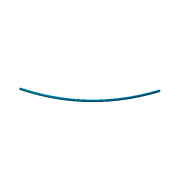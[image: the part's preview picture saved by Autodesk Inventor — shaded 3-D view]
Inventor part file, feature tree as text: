
AUTODESK INVENTOR PART (.ipt)
format: ipt  version: 2016 (Build 200138000, 138)  size: 222,208 bytes
history: native  units: in
note: dims shown in document units (in); Inventor stores cm internally (conversion verified against a paired STEP export)
features: sketch x6, extrude x3, sweep x2, other x2, plane x1
ambient origin geometry x8: Origin, YZ Plane, XZ Plane, XY Plane, X Axis, Y Axis, Z Axis, Center Point
bodies: Body1 (feature_tree)
feature tree (14):
  sweep  "FullSpar"
  sweep  "removeFirstPart"
  extrude  "Extrusion10"  TaperAngle=0.0deg  [1 undecoded]
  extrude  "Extrusion12"  Depth=0.3937in TaperAngle=0.0deg
  sketch  "Sketch21"  dims[d48=0.2756in d49=7.874in d50=0.0in]
  plane  "Work Plane1"
  extrude  "Extrusion13"  Depth=7.874in TaperAngle=0.0deg
  other  "2D Equation Curve1"
  sketch  "Sketch4"  dims[d0=0.0in d1=270.0in d6=2.4803in]
  other  "2D Equation Curve2"
  sketch  "Sketch11"  dims[d7=0.1417in d8=0.0in]
  sketch  "Sketch18"  dims[d19=0.0in d20=76.7717in d21=0.0in]
  sketch  "Sketch20"  dims[d40=1.4961in d41=0.0in d46=0.3937in d47=0.0in]
  sketch  "Sketch22"  dims[d51=6.6929in d52=0.0in d53=0.0in]
note: 1 required parameter value undecoded (feature->parameter linkage not recoverable at this tier; creation-order binding heuristic only, values carry confidence <= 0.55)
